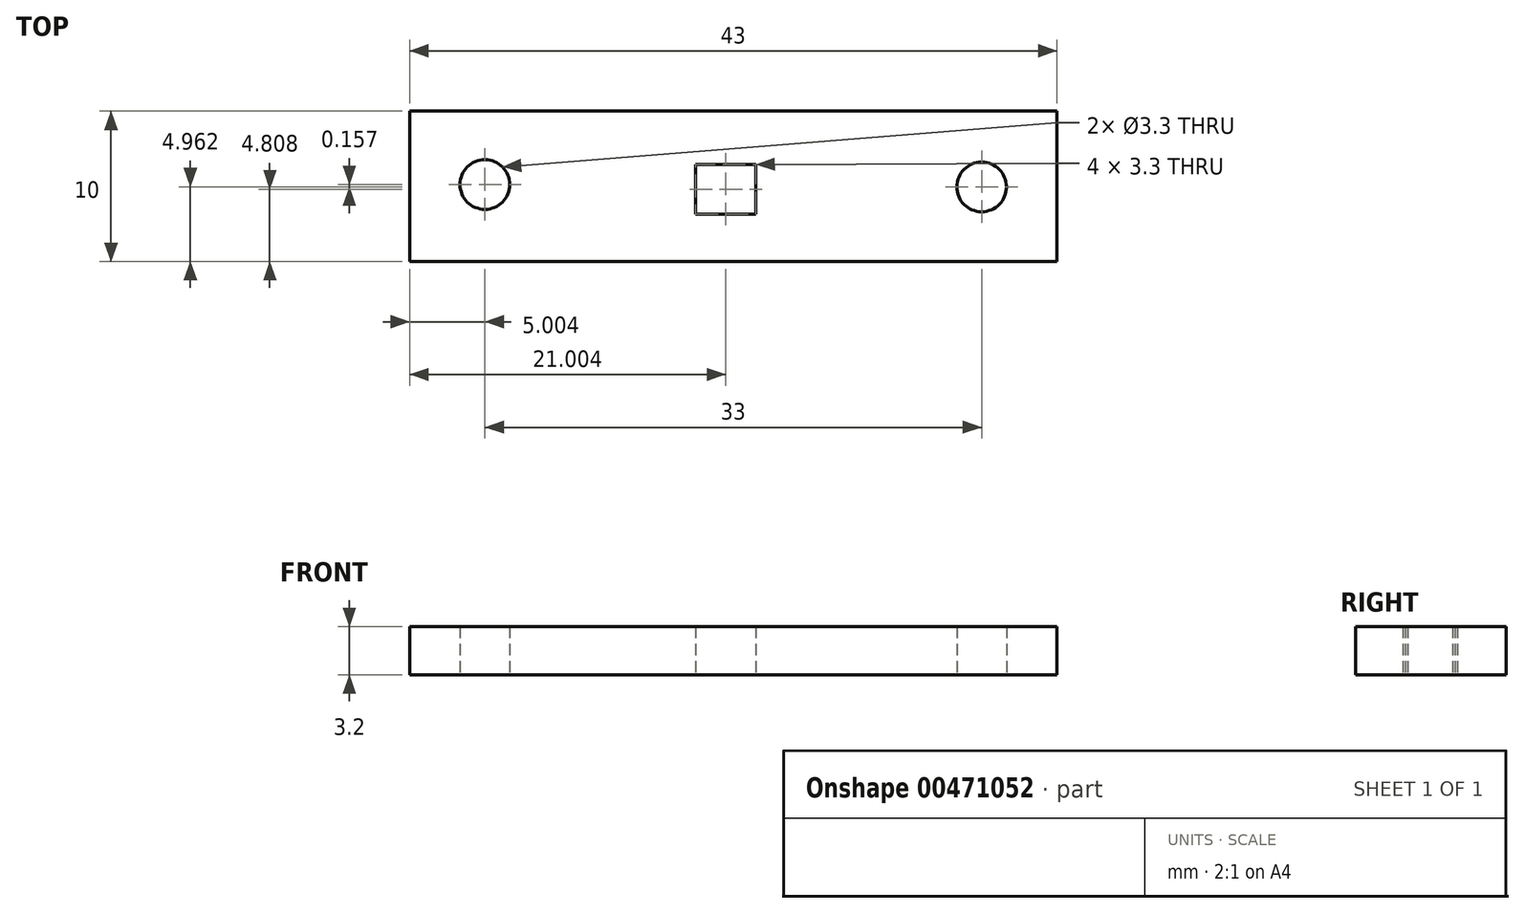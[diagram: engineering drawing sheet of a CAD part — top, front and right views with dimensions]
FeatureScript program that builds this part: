
annotation { "Feature Type Name" : "Feature", "Feature Type Description" : "" }
export const myFeature = defineFeature(function(context is Context, id is Id, definition is map)
    precondition{}
    {
        {
            var Q0;
            Q0=qCreatedBy(makeId("Top.planeOp"),FACE);
            var sketch = newSketch(context, id + "F0", { "sketchPlane" : qUnion([Q0])});
            skLineSegment(sketch, "E0.bottom", {"start": v(-46.17, 16.63) * mm, "end": v(-3.17, 16.63) * mm});
            skLineSegment(sketch, "E0.top", {"start": v(-46.17, 6.63) * mm, "end": v(-3.17, 6.63) * mm});
            skLineSegment(sketch, "E0.left", {"start": v(-46.17, 16.63) * mm, "end": v(-46.17, 6.63) * mm});
            skLineSegment(sketch, "E0.right", {"start": v(-3.17, 16.63) * mm, "end": v(-3.17, 6.63) * mm});
            skCircle(sketch, "E1", {"center": v(-41.17, 11.75) * mm, "radius": 1.65 * mm});
            skCircle(sketch, "E2", {"center": v(-8.17, 11.6) * mm, "radius": 1.65 * mm});
            skLineSegment(sketch, "E3.top", {"start": v(-27.17, 9.79) * mm, "end": v(-23.17, 9.79) * mm});
            skLineSegment(sketch, "E3.left", {"start": v(-27.17, 13.09) * mm, "end": v(-27.17, 9.79) * mm});
            skLineSegment(sketch, "E3.right", {"start": v(-23.17, 13.09) * mm, "end": v(-23.17, 9.79) * mm});
            skLineSegment(sketch, "E4", {"start": v(-27.17, 13.09) * mm, "end": v(-23.17, 13.09) * mm});
            skSolve(sketch);
        }
        {
            var Q0;
            Q0 = qSketchRegion(id + "F0", true);
            extrude(context, id + "F1", {"entities" : qUnion([Q0]), "depth" : 3.2 * mm, "offsetDistance" : 25 * mm});
        }
    });
